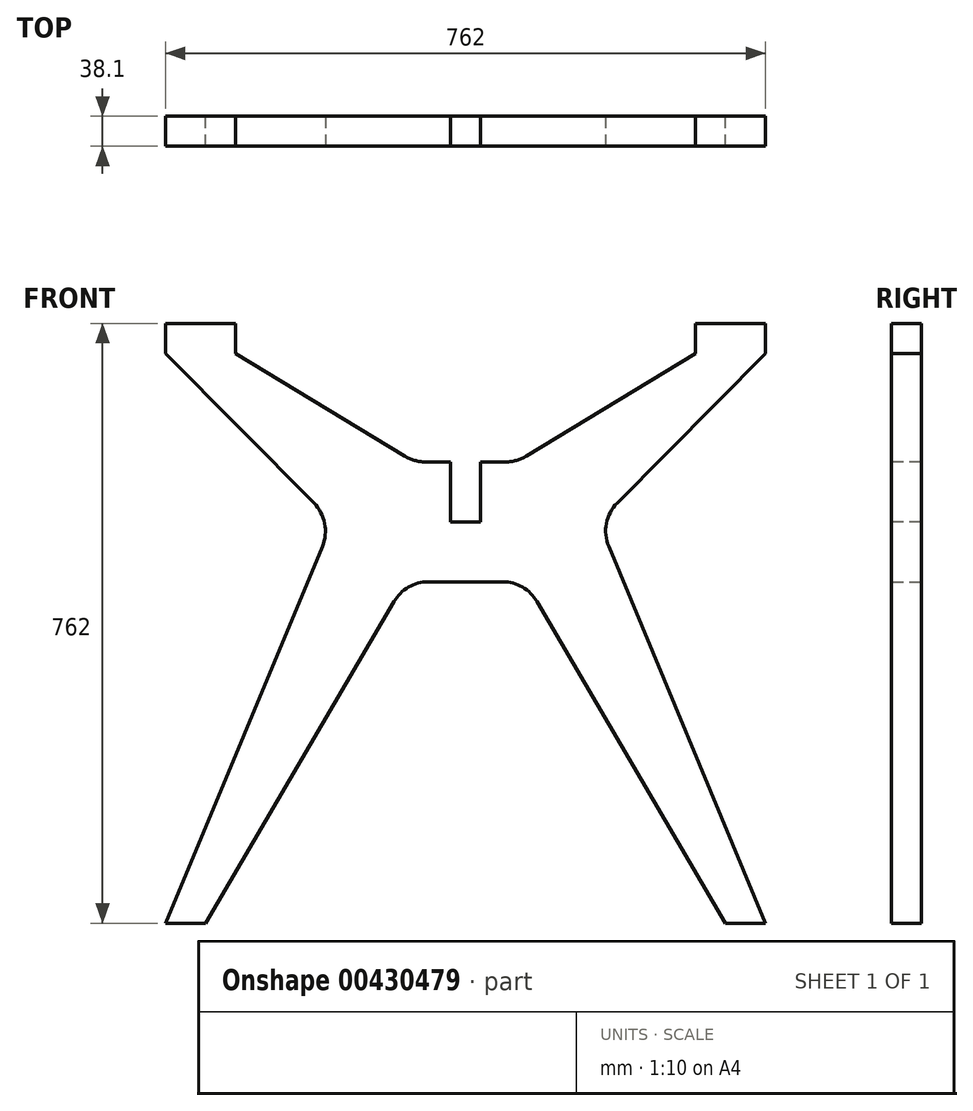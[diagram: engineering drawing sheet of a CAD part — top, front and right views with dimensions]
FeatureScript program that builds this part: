
annotation { "Feature Type Name" : "Feature", "Feature Type Description" : "" }
export const myFeature = defineFeature(function(context is Context, id is Id, definition is map)
    precondition{}
    {
        {
            var Q0;
            Q0=qCreatedBy(makeId("Front.planeOp"),FACE);
            var sketch = newSketch(context, id + "F0", { "sketchPlane" : qUnion([Q0])});
            skLineSegment(sketch, "E0", {"start": v(0, 0) * mm, "end": v(0, 630.74) * mm, "construction": true});
            skLineSegment(sketch, "E1", {"start": v(-19.05, 0) * mm, "end": v(-76.2, 0) * mm});
            skLineSegment(sketch, "E2", {"start": v(-76.2, 0) * mm, "end": v(-330.2, -433.69) * mm});
            skLineSegment(sketch, "E3", {"start": v(-330.2, -433.69) * mm, "end": v(-381, -433.69) * mm});
            skLineSegment(sketch, "E4", {"start": v(-381, -433.69) * mm, "end": v(-168.92, 76.2) * mm});
            skLineSegment(sketch, "E5", {"start": v(-168.92, 76.2) * mm, "end": v(-381, 290.21) * mm});
            skLineSegment(sketch, "E6", {"start": v(-381, 290.21) * mm, "end": v(-292.1, 290.21) * mm});
            skLineSegment(sketch, "E7", {"start": v(-292.1, 290.21) * mm, "end": v(-65.28, 152.4) * mm});
            skLineSegment(sketch, "E8", {"start": v(-65.28, 152.4) * mm, "end": v(0, 152.4) * mm});
            skLineSegment(sketch, "E9.MirrorCS", {"start": v(330.2, -433.69) * mm, "end": v(381, -433.69) * mm});
            skLineSegment(sketch, "E10.MirrorCS", {"start": v(19.05, 0) * mm, "end": v(76.2, 0) * mm});
            skLineSegment(sketch, "E11.MirrorCS", {"start": v(381, 290.21) * mm, "end": v(292.1, 290.21) * mm});
            skLineSegment(sketch, "E12.MirrorCS", {"start": v(168.92, 76.2) * mm, "end": v(381, 290.21) * mm});
            skLineSegment(sketch, "E13.MirrorCS", {"start": v(65.28, 152.4) * mm, "end": v(0, 152.4) * mm});
            skLineSegment(sketch, "E14.MirrorCS", {"start": v(76.2, 0) * mm, "end": v(330.2, -433.69) * mm});
            skLineSegment(sketch, "E15.MirrorCS", {"start": v(292.1, 290.21) * mm, "end": v(65.28, 152.4) * mm});
            skLineSegment(sketch, "E16.MirrorCS", {"start": v(381, -433.69) * mm, "end": v(168.92, 76.2) * mm});
            skLineSegment(sketch, "E17", {"start": v(-19.05, 0) * mm, "end": v(-19.05, 76.2) * mm, "construction": true});
            skLineSegment(sketch, "E18", {"start": v(-19.05, 76.2) * mm, "end": v(0, 76.2) * mm, "construction": true});
            skLineSegment(sketch, "E19", {"start": v(0, 76.2) * mm, "end": v(19.05, 76.2) * mm, "construction": true});
            skLineSegment(sketch, "E20", {"start": v(19.05, 76.2) * mm, "end": v(19.05, 0) * mm, "construction": true});
            skPoint(sketch, "E21.orphan", {"position": v(0, 0) * mm});
            skLineSegment(sketch, "E22", {"start": v(-19.05, 0) * mm, "end": v(19.05, 0) * mm});
            skLineSegment(sketch, "E23", {"start": v(-19.05, 152.4) * mm, "end": v(-19.05, 76.2) * mm, "construction": true});
            skLineSegment(sketch, "E24", {"start": v(19.05, 76.2) * mm, "end": v(19.05, 152.4) * mm, "construction": true});
            skSolve(sketch);
        }
        {
            var Q0;
            Q0=makeQuery(id+"F0.imprint","IMPRINT",FACE,{"disambiguationData":[TD([[makeQuery(id+"F0.imprint","IMPRINT",EDGE,{"derivedFrom":sQuery(id+"F0.wireOp",EDGE,"E1")}),-1.0]])]});
            extrude(context, id + "F1", {"entities" : qUnion([Q0]), "endBound" : BoundingType.SYMMETRIC, "depth" : 38.1 * mm});
        }
        {
            var Q0;
            Q0=makeQuery(id+"F1.opExtrude","SWEPT_EDGE",EDGE,{"disambiguationData":[OSD([sQuery(id+"F0.wireOp",EDGE,"E12.MirrorCS"),sQuery(id+"F0.wireOp",EDGE,"E16.MirrorCS")])]});
            var Q1;
            Q1=makeQuery(id+"F1.opExtrude","SWEPT_EDGE",EDGE,{"disambiguationData":[OSD([sQuery(id+"F0.wireOp",EDGE,"E7"),sQuery(id+"F0.wireOp",EDGE,"E8")])]});
            var Q2;
            Q2=makeQuery(id+"F1.opExtrude","SWEPT_EDGE",EDGE,{"disambiguationData":[OSD([sQuery(id+"F0.wireOp",EDGE,"E13.MirrorCS"),sQuery(id+"F0.wireOp",EDGE,"E15.MirrorCS")])]});
            var Q3;
            Q3=makeQuery(id+"F1.opExtrude","SWEPT_EDGE",EDGE,{"disambiguationData":[OSD([sQuery(id+"F0.wireOp",EDGE,"E4"),sQuery(id+"F0.wireOp",EDGE,"E5")])]});
            var Q4;
            Q4=makeQuery(id+"F1.opExtrude","SWEPT_EDGE",EDGE,{"disambiguationData":[OSD([sQuery(id+"F0.wireOp",EDGE,"E1"),sQuery(id+"F0.wireOp",EDGE,"E2")])]});
            var Q5;
            Q5=makeQuery(id+"F1.opExtrude","SWEPT_EDGE",EDGE,{"disambiguationData":[OSD([sQuery(id+"F0.wireOp",EDGE,"E10.MirrorCS"),sQuery(id+"F0.wireOp",EDGE,"E14.MirrorCS")])]});
            fillet(context, id + "F2", {"entities" : qUnion([Q0, Q1, Q2, Q3, Q4, Q5]), "radius" : 50.8 * mm, "tangentPropagation" : true, "allowEdgeOverflow" : false});
        }
        {
            var Q0;
            Q0=makeQuery(id+"F1.opExtrude","SWEPT_FACE",FACE,{"disambiguationData":[OSD([sQuery(id+"F0.wireOp",EDGE,"E11.MirrorCS")])]});
            var sketch = newSketch(context, id + "F3", { "sketchPlane" : qUnion([Q0])});
            skLineSegment(sketch, "E25.0", {"start": v(292.1, -19.05) * mm, "end": v(292.1, 19.05) * mm});
            skLineSegment(sketch, "E26.0", {"start": v(381, 19.05) * mm, "end": v(292.1, 19.05) * mm});
            skLineSegment(sketch, "E27.0", {"start": v(381, -19.05) * mm, "end": v(381, 19.05) * mm});
            skLineSegment(sketch, "E28.0", {"start": v(381, -19.05) * mm, "end": v(292.1, -19.05) * mm});
            skLineSegment(sketch, "E29.0", {"start": v(-292.1, -19.05) * mm, "end": v(-292.1, 19.05) * mm});
            skLineSegment(sketch, "E30.0", {"start": v(-381, 19.05) * mm, "end": v(-292.1, 19.05) * mm});
            skLineSegment(sketch, "E31.0", {"start": v(-381, -19.05) * mm, "end": v(-381, 19.05) * mm});
            skLineSegment(sketch, "E32.0", {"start": v(-381, -19.05) * mm, "end": v(-292.1, -19.05) * mm});
            skSolve(sketch);
        }
        {
            var Q0;
            Q0=makeQuery(id+"F3.imprint","IMPRINT",FACE,{"disambiguationData":[TD([[makeQuery(id+"F3.imprint","IMPRINT",EDGE,{"derivedFrom":sQuery(id+"F3.wireOp",EDGE,"E29.0")}),1.0]])]});
            var Q1;
            Q1=makeQuery(id+"F3.imprint","IMPRINT",FACE,{"disambiguationData":[TD([[makeQuery(id+"F3.imprint","IMPRINT",EDGE,{"derivedFrom":sQuery(id+"F3.wireOp",EDGE,"E25.0")}),-1.0]])]});
            extrude(context, id + "F4", {"entities" : qUnion([Q0, Q1]), "operationType" : NewBodyOperationType.ADD, "depth" : 38.1 * mm});
        }
        {
            var Q0;
            Q0=makeQuery(id+"F4.boolean.opBoolean","MERGE",FACE,{"derivedFrom":[makeQuery(id+"F1.opExtrude","CAP_FACE",FACE,{"disambiguationData":[OSD([sQuery(id+"F0.wireOp",EDGE,"E1"),sQuery(id+"F0.wireOp",EDGE,"E2"),sQuery(id+"F0.wireOp",EDGE,"E3"),sQuery(id+"F0.wireOp",EDGE,"E4"),sQuery(id+"F0.wireOp",EDGE,"E5"),sQuery(id+"F0.wireOp",EDGE,"E6"),sQuery(id+"F0.wireOp",EDGE,"E7"),sQuery(id+"F0.wireOp",EDGE,"E8"),sQuery(id+"F0.wireOp",EDGE,"E9.MirrorCS"),sQuery(id+"F0.wireOp",EDGE,"E10.MirrorCS"),sQuery(id+"F0.wireOp",EDGE,"E11.MirrorCS"),sQuery(id+"F0.wireOp",EDGE,"E12.MirrorCS"),sQuery(id+"F0.wireOp",EDGE,"E13.MirrorCS"),sQuery(id+"F0.wireOp",EDGE,"E14.MirrorCS"),sQuery(id+"F0.wireOp",EDGE,"E15.MirrorCS"),sQuery(id+"F0.wireOp",EDGE,"E16.MirrorCS"),sQuery(id+"F0.wireOp",EDGE,"E22")])],"isStart":false}),makeQuery(id+"F4.opExtrude","SWEPT_FACE",FACE,{"disambiguationData":[OSD([sQuery(id+"F3.wireOp",EDGE,"E28.0")])]}),makeQuery(id+"F4.opExtrude","SWEPT_FACE",FACE,{"disambiguationData":[OSD([sQuery(id+"F3.wireOp",EDGE,"E32.0")])]})]});
            var sketch = newSketch(context, id + "F5", { "sketchPlane" : qUnion([Q0])});
            skLineSegment(sketch, "E33.bottom", {"start": v(-19.05, 152.4) * mm, "end": v(19.05, 152.4) * mm});
            skLineSegment(sketch, "E33.top", {"start": v(-19.05, 76.2) * mm, "end": v(19.05, 76.2) * mm});
            skLineSegment(sketch, "E33.left", {"start": v(-19.05, 76.2) * mm, "end": v(-19.05, 152.4) * mm});
            skLineSegment(sketch, "E33.right", {"start": v(19.05, 76.2) * mm, "end": v(19.05, 152.4) * mm});
            skSolve(sketch);
        }
        {
            var Q0;
            Q0=makeQuery(id+"F5.imprint","IMPRINT",FACE,{"disambiguationData":[TD([[makeQuery(id+"F5.imprint","IMPRINT",EDGE,{"derivedFrom":sQuery(id+"F5.wireOp",EDGE,"E33.bottom")}),1.0]])]});
            extrude(context, id + "F6", {"entities" : qUnion([Q0]), "operationType" : NewBodyOperationType.REMOVE, "endBound" : BoundingType.THROUGH_ALL, "oppositeDirection" : true, "depth" : 25.4 * mm});
        }
    });
